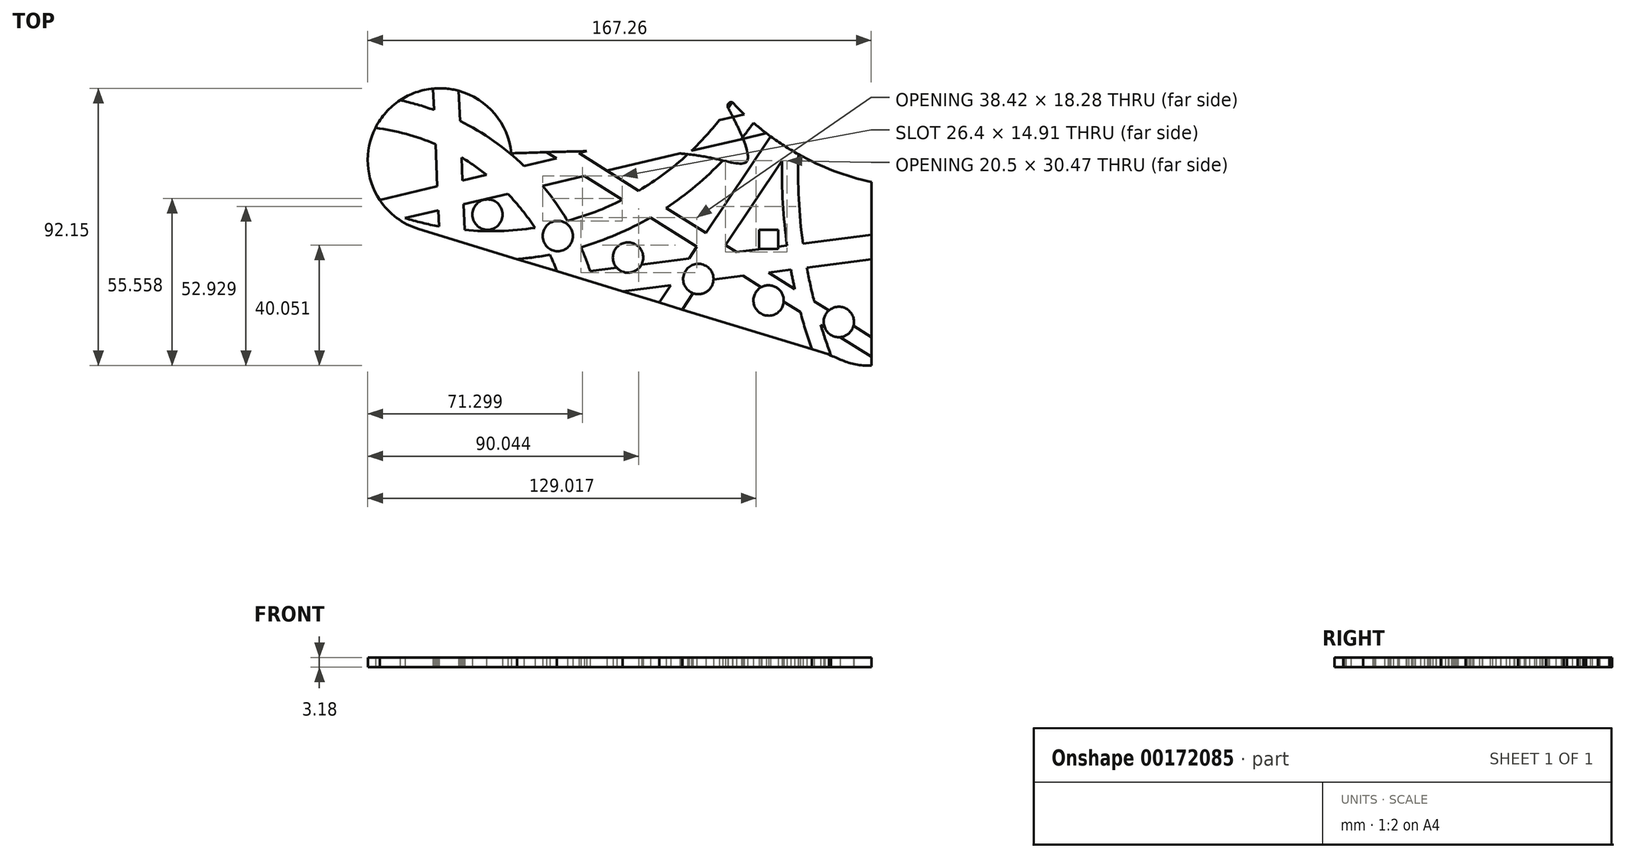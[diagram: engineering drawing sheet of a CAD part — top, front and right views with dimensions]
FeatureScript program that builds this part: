
annotation { "Feature Type Name" : "Feature", "Feature Type Description" : "" }
export const myFeature = defineFeature(function(context is Context, id is Id, definition is map)
    precondition{}
    {
        {
            var Q0;
            Q0=qCreatedBy(makeId("Top.planeOp"),FACE);
            var sketch = newSketch(context, id + "F0", { "sketchPlane" : qUnion([Q0])});
            skArc(sketch, "E0", {"start": v(-90.46, -15.28) * mm, "mid": v(-14.2, -9.68) * mm, "end": v(38.46, 45.77) * mm});
            skArc(sketch, "E1.0", {"start": v(-100.3, -1.2) * mm, "mid": v(-24.88, -3.77) * mm, "end": v(29.26, 48.8) * mm});
            skArc(sketch, "E2", {"start": v(51.31, 64.63) * mm, "mid": v(42.5, 3.49) * mm, "end": v(55.46, -56.9) * mm});
            skArc(sketch, "E3.0", {"start": v(46.25, 66.31) * mm, "mid": v(37.17, 3.3) * mm, "end": v(50.52, -58.93) * mm});
            skArc(sketch, "E4", {"start": v(-33.41, -40.98) * mm, "mid": v(-60.63, 8.15) * mm, "end": v(-114.4, 24.36) * mm});
            skArc(sketch, "E5.0", {"start": v(-23.07, -39.74) * mm, "mid": v(-54.1, 16.25) * mm, "end": v(-115.38, 34.73) * mm});
            skLineSegment(sketch, "E6.0", {"start": v(52.65, -51.2) * mm, "end": v(-83.61, -9.54) * mm});
            skArc(sketch, "E6.1", {"start": v(-52.83, 15.6) * mm, "mid": v(-91.75, 31.83) * mm, "end": v(-83.61, -9.54) * mm});
            skFitSpline(sketch, "E6.5", {"points": [v(52.65, -51.2) * mm, v(64.8, -54.91) * mm, v(80.38, -50.62) * mm, v(85.15, -44.27) * mm]});
            skLineSegment(sketch, "E6.6", {"start": v(66.1, 6.22) * mm, "end": v(66.1, -52.4) * mm});
            skPoint(sketch, "E7.visualSharp", {"position": v(13.9, 42.17) * mm});
            skArc(sketch, "E8", {"start": v(12.87, 42.18) * mm, "mid": v(44.36, 14.28) * mm, "end": v(85.15, 3.99) * mm});
            skFitSpline(sketch, "E9", {"points": [v(-52.83, 15.6) * mm, v(12.87, 42.18) * mm], "startDerivative": vector(194.61, -3.65) * mm, "endDerivative": vector(-37.72, 87.36) * mm});
            skLineSegment(sketch, "E10", {"start": v(66.73, 6.07) * mm, "end": v(66.73, -50.68) * mm});
            skLineSegment(sketch, "E11", {"start": v(66.73, -50.68) * mm, "end": v(66.73, -55.63) * mm});
            skArc(sketch, "E12", {"start": v(66.1, -52.4) * mm, "mid": v(66.43, -52.34) * mm, "end": v(66.73, -52.2) * mm});
            skSolve(sketch);
        }
        {
            var Q0;
            Q0=qCreatedBy(makeId("Top.planeOp"),FACE);
            var sketch = newSketch(context, id + "F1", { "sketchPlane" : qUnion([Q0])});
            skLineSegment(sketch, "E13", {"start": v(41.28, 19.45) * mm, "end": v(0, -42.12) * mm});
            skLineSegment(sketch, "E14", {"start": v(0, -42.12) * mm, "end": v(-6.32, -37.88) * mm});
            skLineSegment(sketch, "E15", {"start": v(-6.32, -37.88) * mm, "end": v(38.05, 28.32) * mm});
            skLineSegment(sketch, "E16", {"start": v(38.05, 28.32) * mm, "end": v(41.28, 19.45) * mm});
            skLineSegment(sketch, "E17", {"start": v(40.9, -75.03) * mm, "end": v(46.22, -72.68) * mm});
            skLineSegment(sketch, "E18", {"start": v(-56.42, -35.5) * mm, "end": v(132.52, -11.1) * mm});
            skLineSegment(sketch, "E19", {"start": v(132.52, -11.1) * mm, "end": v(131.24, -3.12) * mm});
            skLineSegment(sketch, "E20", {"start": v(131.24, -3.12) * mm, "end": v(-56.79, -27.4) * mm});
            skLineSegment(sketch, "E21", {"start": v(-56.79, -27.4) * mm, "end": v(-56.42, -35.5) * mm});
            skLineSegment(sketch, "E22", {"start": v(-71.95, 73.85) * mm, "end": v(-66.69, -48.5) * mm});
            skLineSegment(sketch, "E23", {"start": v(-66.69, -48.5) * mm, "end": v(-75.13, -48.86) * mm});
            skLineSegment(sketch, "E24", {"start": v(-75.13, -48.86) * mm, "end": v(-80.24, 69.83) * mm});
            skLineSegment(sketch, "E25", {"start": v(-80.24, 69.83) * mm, "end": v(-71.95, 73.85) * mm});
            skLineSegment(sketch, "E26", {"start": v(70.66, -54.45) * mm, "end": v(-45.44, 18.7) * mm});
            skLineSegment(sketch, "E27", {"start": v(-45.44, 18.7) * mm, "end": v(-42.5, 23.35) * mm});
            skLineSegment(sketch, "E28", {"start": v(-42.5, 23.35) * mm, "end": v(73.52, -49.75) * mm});
            skLineSegment(sketch, "E29", {"start": v(73.52, -49.75) * mm, "end": v(70.66, -54.45) * mm});
            skLineSegment(sketch, "E30", {"start": v(56.6, 28.12) * mm, "end": v(-113.4, -11.85) * mm});
            skLineSegment(sketch, "E31", {"start": v(-113.4, -11.85) * mm, "end": v(-115.19, -4.23) * mm});
            skLineSegment(sketch, "E32", {"start": v(-115.19, -4.23) * mm, "end": v(55.1, 35.8) * mm});
            skLineSegment(sketch, "E33", {"start": v(55.1, 35.8) * mm, "end": v(56.6, 28.12) * mm});
            skArc(sketch, "E34.0", {"start": v(-90.46, -15.28) * mm, "mid": v(-14.2, -9.68) * mm, "end": v(38.46, 45.77) * mm});
            skArc(sketch, "E34.1", {"start": v(-100.3, -1.2) * mm, "mid": v(-24.88, -3.77) * mm, "end": v(29.26, 48.8) * mm});
            skArc(sketch, "E34.2", {"start": v(51.31, 64.63) * mm, "mid": v(42.5, 3.49) * mm, "end": v(55.46, -56.9) * mm});
            skArc(sketch, "E34.3", {"start": v(46.25, 66.31) * mm, "mid": v(37.17, 3.3) * mm, "end": v(50.52, -58.93) * mm});
            skArc(sketch, "E34.4", {"start": v(-33.41, -40.98) * mm, "mid": v(-60.63, 8.15) * mm, "end": v(-114.4, 24.36) * mm});
            skArc(sketch, "E34.5", {"start": v(-23.07, -39.74) * mm, "mid": v(-54.1, 16.25) * mm, "end": v(-115.38, 34.73) * mm});
            skArc(sketch, "E35.0", {"start": v(-52.83, 15.6) * mm, "mid": v(-91.75, 31.83) * mm, "end": v(-83.61, -9.54) * mm});
            skFitSpline(sketch, "E35.1", {"points": [v(-52.83, 15.6) * mm, v(12.04, 14.39) * mm, v(25.44, 13.06) * mm, v(12.87, 42.18) * mm]});
            skArc(sketch, "E35.2", {"start": v(12.87, 42.18) * mm, "mid": v(44.36, 14.28) * mm, "end": v(85.15, 3.99) * mm});
            skLineSegment(sketch, "E35.3", {"start": v(66.1, 6.22) * mm, "end": v(66.1, -52.4) * mm});
            skFitSpline(sketch, "E35.4", {"points": [v(52.65, -51.2) * mm, v(64.8, -54.91) * mm, v(80.38, -50.62) * mm, v(85.15, -44.27) * mm]});
            skLineSegment(sketch, "E35.5", {"start": v(52.65, -51.2) * mm, "end": v(-83.61, -9.54) * mm});
            skLineSegment(sketch, "E36.0", {"start": v(66.73, 6.07) * mm, "end": v(66.73, -50.68) * mm});
            skLineSegment(sketch, "E37.0", {"start": v(66.73, -50.68) * mm, "end": v(66.73, -55.63) * mm});
            skArc(sketch, "E38.0", {"start": v(66.1, -52.4) * mm, "mid": v(66.43, -52.34) * mm, "end": v(66.73, -52.2) * mm});
            skSolve(sketch);
        }
        {
            var Q0;
            {var subQ0=sQuery(id+"F1.wireOp",EDGE,"E35.3");var subQ1=sQuery(id+"F1.wireOp",EDGE,"E26");var subQ2=makeQuery(id+"F1.imprint","INTERSECT",VERTEX,{"derivedFrom":[subQ1,subQ0]});Q0=makeQuery(id+"F1.imprint","IMPRINT",FACE,{"disambiguationData":[TD([[makeQuery(id+"F1.imprint","IMPRINT",EDGE,{"disambiguationData":[TD([[subQ2,-1.0]])],"derivedFrom":subQ1}),-1.0]])]});}
            var Q1;
            {var subQ0=sQuery(id+"F1.wireOp",EDGE,"E37.0");var subQ6=sQuery(id+"F1.wireOp",EDGE,"E26");var subQ9=makeQuery(id+"F1.imprint","INTERSECT",VERTEX,{"derivedFrom":[subQ6,subQ0]});Q1=makeQuery(id+"F1.imprint","IMPRINT",FACE,{"disambiguationData":[TD([[makeQuery(id+"F1.imprint","IMPRINT",EDGE,{"disambiguationData":[TD([[subQ9,-1.0]])],"derivedFrom":subQ6}),-1.0]])]});}
            var Q2;
            {var subQ0=sQuery(id+"F1.wireOp",EDGE,"E36.0");var subQ1=sQuery(id+"F1.wireOp",EDGE,"E18");var subQ2=makeQuery(id+"F1.imprint","INTERSECT",VERTEX,{"derivedFrom":[subQ1,subQ0]});Q2=makeQuery(id+"F1.imprint","IMPRINT",FACE,{"disambiguationData":[TD([[makeQuery(id+"F1.imprint","IMPRINT",EDGE,{"disambiguationData":[TD([[subQ2,1.0]])],"derivedFrom":subQ1}),1.0]])]});}
            var Q3;
            {var subQ0=sQuery(id+"F1.wireOp",EDGE,"E34.2");var subQ1=sQuery(id+"F1.wireOp",EDGE,"E18");var subQ2=makeQuery(id+"F1.imprint","INTERSECT",VERTEX,{"derivedFrom":[subQ1,subQ0]});Q3=makeQuery(id+"F1.imprint","IMPRINT",FACE,{"disambiguationData":[TD([[makeQuery(id+"F1.imprint","IMPRINT",EDGE,{"disambiguationData":[TD([[subQ2,-1.0]])],"derivedFrom":subQ1}),1.0]])]});}
            var Q4;
            {var subQ0=sQuery(id+"F1.wireOp",EDGE,"E34.2");var subQ1=sQuery(id+"F1.wireOp",EDGE,"E13");var subQ2=makeQuery(id+"F1.imprint","INTERSECT",VERTEX,{"derivedFrom":[subQ1,subQ0]});Q4=makeQuery(id+"F1.imprint","IMPRINT",FACE,{"disambiguationData":[TD([[makeQuery(id+"F1.imprint","IMPRINT",EDGE,{"disambiguationData":[TD([[subQ2,-1.0]])],"derivedFrom":subQ1}),-1.0]])]});}
            var Q5;
            {var subQ0=sQuery(id+"F1.wireOp",EDGE,"E34.3");var subQ1=sQuery(id+"F1.wireOp",EDGE,"E13");var subQ2=makeQuery(id+"F1.imprint","INTERSECT",VERTEX,{"derivedFrom":[subQ1,subQ0]});Q5=makeQuery(id+"F1.imprint","IMPRINT",FACE,{"disambiguationData":[TD([[makeQuery(id+"F1.imprint","IMPRINT",EDGE,{"disambiguationData":[TD([[subQ2,-1.0]])],"derivedFrom":subQ1}),-1.0]])]});}
            var Q6;
            {var subQ0=sQuery(id+"F1.wireOp",EDGE,"E34.2");var subQ1=sQuery(id+"F1.wireOp",EDGE,"E13");var subQ2=makeQuery(id+"F1.imprint","INTERSECT",VERTEX,{"derivedFrom":[subQ1,subQ0]});Q6=makeQuery(id+"F1.imprint","IMPRINT",FACE,{"disambiguationData":[TD([[makeQuery(id+"F1.imprint","IMPRINT",EDGE,{"disambiguationData":[TD([[subQ2,-1.0]])],"derivedFrom":subQ1}),1.0]])]});}
            var Q7;
            {var subQ0=sQuery(id+"F1.wireOp",EDGE,"E34.3");var subQ1=sQuery(id+"F1.wireOp",EDGE,"E18");var subQ2=makeQuery(id+"F1.imprint","INTERSECT",VERTEX,{"derivedFrom":[subQ1,subQ0]});Q7=makeQuery(id+"F1.imprint","IMPRINT",FACE,{"disambiguationData":[TD([[makeQuery(id+"F1.imprint","IMPRINT",EDGE,{"disambiguationData":[TD([[subQ2,-1.0]])],"derivedFrom":subQ1}),1.0]])]});}
            var Q8;
            {var subQ0=sQuery(id+"F1.wireOp",EDGE,"E34.3");var subQ1=sQuery(id+"F1.wireOp",EDGE,"E18");var subQ2=makeQuery(id+"F1.imprint","INTERSECT",VERTEX,{"derivedFrom":[subQ1,subQ0]});Q8=makeQuery(id+"F1.imprint","IMPRINT",FACE,{"disambiguationData":[TD([[makeQuery(id+"F1.imprint","IMPRINT",EDGE,{"disambiguationData":[TD([[subQ2,-1.0]])],"derivedFrom":subQ1}),-1.0]])]});}
            var Q9;
            {var subQ0=sQuery(id+"F1.wireOp",EDGE,"E34.2");var subQ1=sQuery(id+"F1.wireOp",EDGE,"E26");var subQ2=makeQuery(id+"F1.imprint","INTERSECT",VERTEX,{"derivedFrom":[subQ1,subQ0]});Q9=makeQuery(id+"F1.imprint","IMPRINT",FACE,{"disambiguationData":[TD([[makeQuery(id+"F1.imprint","IMPRINT",EDGE,{"disambiguationData":[TD([[subQ2,-1.0]])],"derivedFrom":subQ1}),-1.0]])]});}
            var Q10;
            {var subQ3=sQuery(id+"F1.wireOp",EDGE,"E34.2");var subQ7=sQuery(id+"F1.wireOp",EDGE,"E26");var subQ9=makeQuery(id+"F1.imprint","INTERSECT",VERTEX,{"derivedFrom":[subQ7,subQ3]});Q10=makeQuery(id+"F1.imprint","IMPRINT",FACE,{"disambiguationData":[TD([[makeQuery(id+"F1.imprint","IMPRINT",EDGE,{"disambiguationData":[TD([[subQ9,-1.0]])],"derivedFrom":subQ7}),1.0]])]});}
            var Q11;
            {var subQ0=sQuery(id+"F1.wireOp",EDGE,"E26");var subQ1=sQuery(id+"F1.wireOp",EDGE,"E18");var subQ2=makeQuery(id+"F1.imprint","INTERSECT",VERTEX,{"derivedFrom":[subQ1,subQ0]});Q11=makeQuery(id+"F1.imprint","IMPRINT",FACE,{"disambiguationData":[TD([[makeQuery(id+"F1.imprint","IMPRINT",EDGE,{"disambiguationData":[TD([[subQ2,-1.0]])],"derivedFrom":subQ1}),-1.0]])]});}
            var Q12;
            {var subQ0=sQuery(id+"F1.wireOp",EDGE,"E28");var subQ1=sQuery(id+"F1.wireOp",EDGE,"E18");var subQ2=makeQuery(id+"F1.imprint","INTERSECT",VERTEX,{"derivedFrom":[subQ1,subQ0]});Q12=makeQuery(id+"F1.imprint","IMPRINT",FACE,{"disambiguationData":[TD([[makeQuery(id+"F1.imprint","IMPRINT",EDGE,{"disambiguationData":[TD([[subQ2,-1.0]])],"derivedFrom":subQ1}),1.0]])]});}
            var Q13;
            {var subQ0=sQuery(id+"F1.wireOp",EDGE,"E20");var subQ1=sQuery(id+"F1.wireOp",EDGE,"E13");var subQ2=makeQuery(id+"F1.imprint","INTERSECT",VERTEX,{"derivedFrom":[subQ1,subQ0]});Q13=makeQuery(id+"F1.imprint","IMPRINT",FACE,{"disambiguationData":[TD([[makeQuery(id+"F1.imprint","IMPRINT",EDGE,{"disambiguationData":[TD([[subQ2,-1.0]])],"derivedFrom":subQ1}),1.0]])]});}
            var Q14;
            {var subQ0=sQuery(id+"F1.wireOp",EDGE,"E28");var subQ1=sQuery(id+"F1.wireOp",EDGE,"E13");var subQ2=makeQuery(id+"F1.imprint","INTERSECT",VERTEX,{"derivedFrom":[subQ1,subQ0]});Q14=makeQuery(id+"F1.imprint","IMPRINT",FACE,{"disambiguationData":[TD([[makeQuery(id+"F1.imprint","IMPRINT",EDGE,{"disambiguationData":[TD([[subQ2,-1.0]])],"derivedFrom":subQ1}),1.0]])]});}
            var Q15;
            {var subQ1=sQuery(id+"F1.wireOp",EDGE,"E13");var subQ7=sQuery(id+"F1.wireOp",EDGE,"E28");var subQ9=makeQuery(id+"F1.imprint","INTERSECT",VERTEX,{"derivedFrom":[subQ1,subQ7]});Q15=makeQuery(id+"F1.imprint","IMPRINT",FACE,{"disambiguationData":[TD([[makeQuery(id+"F1.imprint","IMPRINT",EDGE,{"disambiguationData":[TD([[subQ9,-1.0]])],"derivedFrom":subQ1}),-1.0]])]});}
            var Q16;
            {var subQ0=sQuery(id+"F1.wireOp",EDGE,"E26");var subQ1=sQuery(id+"F1.wireOp",EDGE,"E13");var subQ2=makeQuery(id+"F1.imprint","INTERSECT",VERTEX,{"derivedFrom":[subQ1,subQ0]});Q16=makeQuery(id+"F1.imprint","IMPRINT",FACE,{"disambiguationData":[TD([[makeQuery(id+"F1.imprint","IMPRINT",EDGE,{"disambiguationData":[TD([[subQ2,-1.0]])],"derivedFrom":subQ1}),1.0]])]});}
            var Q17;
            {var subQ0=sQuery(id+"F1.wireOp",EDGE,"E20");var subQ1=sQuery(id+"F1.wireOp",EDGE,"E13");var subQ2=makeQuery(id+"F1.imprint","INTERSECT",VERTEX,{"derivedFrom":[subQ1,subQ0]});Q17=makeQuery(id+"F1.imprint","IMPRINT",FACE,{"disambiguationData":[TD([[makeQuery(id+"F1.imprint","IMPRINT",EDGE,{"disambiguationData":[TD([[subQ2,-1.0]])],"derivedFrom":subQ1}),-1.0]])]});}
            var Q18;
            {var subQ1=sQuery(id+"F1.wireOp",EDGE,"E13");var subQ7=sQuery(id+"F1.wireOp",EDGE,"E26");var subQ9=makeQuery(id+"F1.imprint","INTERSECT",VERTEX,{"derivedFrom":[subQ1,subQ7]});Q18=makeQuery(id+"F1.imprint","IMPRINT",FACE,{"disambiguationData":[TD([[makeQuery(id+"F1.imprint","IMPRINT",EDGE,{"disambiguationData":[TD([[subQ9,-1.0]])],"derivedFrom":subQ1}),-1.0]])]});}
            var Q19;
            {var subQ0=sQuery(id+"F1.wireOp",EDGE,"E20");var subQ1=sQuery(id+"F1.wireOp",EDGE,"E15");var subQ2=makeQuery(id+"F1.imprint","INTERSECT",VERTEX,{"derivedFrom":[subQ1,subQ0]});Q19=makeQuery(id+"F1.imprint","IMPRINT",FACE,{"disambiguationData":[TD([[makeQuery(id+"F1.imprint","IMPRINT",EDGE,{"disambiguationData":[TD([[subQ2,-1.0]])],"derivedFrom":subQ1}),-1.0]])]});}
            var Q20;
            {var subQ0=sQuery(id+"F1.wireOp",EDGE,"E35.5");var subQ1=sQuery(id+"F1.wireOp",EDGE,"E13");var subQ2=makeQuery(id+"F1.imprint","INTERSECT",VERTEX,{"derivedFrom":[subQ1,subQ0]});Q20=makeQuery(id+"F1.imprint","IMPRINT",FACE,{"disambiguationData":[TD([[makeQuery(id+"F1.imprint","IMPRINT",EDGE,{"disambiguationData":[TD([[subQ2,1.0]])],"derivedFrom":subQ1}),-1.0]])]});}
            var Q21;
            {var subQ1=sQuery(id+"F1.wireOp",EDGE,"E18");var subQ3=sQuery(id+"F1.wireOp",EDGE,"E15");var subQ4=makeQuery(id+"F1.imprint","INTERSECT",VERTEX,{"derivedFrom":[subQ3,subQ1]});Q21=makeQuery(id+"F1.imprint","IMPRINT",FACE,{"disambiguationData":[TD([[makeQuery(id+"F1.imprint","IMPRINT",EDGE,{"disambiguationData":[TD([[subQ4,-1.0]])],"derivedFrom":subQ3}),1.0]])]});}
            var Q22;
            {var subQ0=sQuery(id+"F1.wireOp",EDGE,"E26");var subQ1=sQuery(id+"F1.wireOp",EDGE,"E15");var subQ2=makeQuery(id+"F1.imprint","INTERSECT",VERTEX,{"derivedFrom":[subQ1,subQ0]});Q22=makeQuery(id+"F1.imprint","IMPRINT",FACE,{"disambiguationData":[TD([[makeQuery(id+"F1.imprint","IMPRINT",EDGE,{"disambiguationData":[TD([[subQ2,-1.0]])],"derivedFrom":subQ1}),1.0]])]});}
            var Q23;
            {var subQ0=sQuery(id+"F1.wireOp",EDGE,"E34.1");var subQ1=sQuery(id+"F1.wireOp",EDGE,"E28");var subQ2=makeQuery(id+"F1.imprint","INTERSECT",VERTEX,{"derivedFrom":[subQ1,subQ0]});Q23=makeQuery(id+"F1.imprint","IMPRINT",FACE,{"disambiguationData":[TD([[makeQuery(id+"F1.imprint","IMPRINT",EDGE,{"disambiguationData":[TD([[subQ2,-1.0]])],"derivedFrom":subQ1}),1.0]])]});}
            var Q24;
            {var subQ1=sQuery(id+"F1.wireOp",EDGE,"E30");var subQ9=sQuery(id+"F1.wireOp",EDGE,"E34.0");var subQ10=makeQuery(id+"F1.imprint","INTERSECT",VERTEX,{"derivedFrom":[subQ1,subQ9]});Q24=makeQuery(id+"F1.imprint","IMPRINT",FACE,{"disambiguationData":[TD([[makeQuery(id+"F1.imprint","IMPRINT",EDGE,{"disambiguationData":[TD([[subQ10,-1.0]])],"derivedFrom":subQ1}),-1.0]])]});}
            var Q25;
            {var subQ0=sQuery(id+"F1.wireOp",EDGE,"E35.2");var subQ1=sQuery(id+"F1.wireOp",EDGE,"E32");var subQ2=makeQuery(id+"F1.imprint","INTERSECT",VERTEX,{"derivedFrom":[subQ1,subQ0]});Q25=makeQuery(id+"F1.imprint","IMPRINT",FACE,{"disambiguationData":[TD([[makeQuery(id+"F1.imprint","IMPRINT",EDGE,{"disambiguationData":[TD([[subQ2,1.0]])],"derivedFrom":subQ1}),1.0]])]});}
            var Q26;
            {var subQ0=sQuery(id+"F1.wireOp",EDGE,"E35.1");var subQ1=sQuery(id+"F1.wireOp",EDGE,"E28");var subQ2=makeQuery(id+"F1.imprint","INTERSECT",VERTEX,{"derivedFrom":[subQ1,subQ0]});Q26=makeQuery(id+"F1.imprint","IMPRINT",FACE,{"disambiguationData":[TD([[makeQuery(id+"F1.imprint","IMPRINT",EDGE,{"disambiguationData":[TD([[subQ2,-1.0]])],"derivedFrom":subQ1}),1.0]])]});}
            var Q27;
            {var subQ0=sQuery(id+"F1.wireOp",EDGE,"E34.0");var subQ1=sQuery(id+"F1.wireOp",EDGE,"E26");var subQ2=makeQuery(id+"F1.imprint","INTERSECT",VERTEX,{"derivedFrom":[subQ1,subQ0]});Q27=makeQuery(id+"F1.imprint","IMPRINT",FACE,{"disambiguationData":[TD([[makeQuery(id+"F1.imprint","IMPRINT",EDGE,{"disambiguationData":[TD([[subQ2,-1.0]])],"derivedFrom":subQ1}),-1.0]])]});}
            var Q28;
            {var subQ0=sQuery(id+"F1.wireOp",EDGE,"E34.1");var subQ1=sQuery(id+"F1.wireOp",EDGE,"E26");var subQ2=makeQuery(id+"F1.imprint","INTERSECT",VERTEX,{"derivedFrom":[subQ1,subQ0]});Q28=makeQuery(id+"F1.imprint","IMPRINT",FACE,{"disambiguationData":[TD([[makeQuery(id+"F1.imprint","IMPRINT",EDGE,{"disambiguationData":[TD([[subQ2,-1.0]])],"derivedFrom":subQ1}),-1.0]])]});}
            var Q29;
            {var subQ0=sQuery(id+"F1.wireOp",EDGE,"E30");var subQ1=sQuery(id+"F1.wireOp",EDGE,"E26");var subQ2=makeQuery(id+"F1.imprint","INTERSECT",VERTEX,{"derivedFrom":[subQ1,subQ0]});Q29=makeQuery(id+"F1.imprint","IMPRINT",FACE,{"disambiguationData":[TD([[makeQuery(id+"F1.imprint","IMPRINT",EDGE,{"disambiguationData":[TD([[subQ2,-1.0]])],"derivedFrom":subQ1}),-1.0]])]});}
            var Q30;
            {var subQ0=sQuery(id+"F1.wireOp",EDGE,"E35.1");var subQ1=sQuery(id+"F1.wireOp",EDGE,"E26");var subQ2=makeQuery(id+"F1.imprint","INTERSECT",VERTEX,{"derivedFrom":[subQ1,subQ0]});Q30=makeQuery(id+"F1.imprint","IMPRINT",FACE,{"disambiguationData":[TD([[makeQuery(id+"F1.imprint","IMPRINT",EDGE,{"disambiguationData":[TD([[subQ2,1.0]])],"derivedFrom":subQ1}),-1.0]])]});}
            var Q31;
            {var subQ0=sQuery(id+"F1.wireOp",EDGE,"E30");var subQ1=sQuery(id+"F1.wireOp",EDGE,"E26");var subQ2=makeQuery(id+"F1.imprint","INTERSECT",VERTEX,{"derivedFrom":[subQ1,subQ0]});Q31=makeQuery(id+"F1.imprint","IMPRINT",FACE,{"disambiguationData":[TD([[makeQuery(id+"F1.imprint","IMPRINT",EDGE,{"disambiguationData":[TD([[subQ2,-1.0]])],"derivedFrom":subQ1}),1.0]])]});}
            var Q32;
            {var subQ0=sQuery(id+"F1.wireOp",EDGE,"E34.0");var subQ1=sQuery(id+"F1.wireOp",EDGE,"E26");var subQ2=makeQuery(id+"F1.imprint","INTERSECT",VERTEX,{"derivedFrom":[subQ1,subQ0]});Q32=makeQuery(id+"F1.imprint","IMPRINT",FACE,{"disambiguationData":[TD([[makeQuery(id+"F1.imprint","IMPRINT",EDGE,{"disambiguationData":[TD([[subQ2,-1.0]])],"derivedFrom":subQ1}),1.0]])]});}
            var Q33;
            {var subQ0=sQuery(id+"F1.wireOp",EDGE,"E34.5");var subQ1=sQuery(id+"F1.wireOp",EDGE,"E20");var subQ2=makeQuery(id+"F1.imprint","INTERSECT",VERTEX,{"derivedFrom":[subQ1,subQ0]});Q33=makeQuery(id+"F1.imprint","IMPRINT",FACE,{"disambiguationData":[TD([[makeQuery(id+"F1.imprint","IMPRINT",EDGE,{"disambiguationData":[TD([[subQ2,-1.0]])],"derivedFrom":subQ1}),1.0]])]});}
            var Q34;
            {var subQ5=sQuery(id+"F1.wireOp",EDGE,"E34.5");var subQ7=sQuery(id+"F1.wireOp",EDGE,"E20");var subQ8=makeQuery(id+"F1.imprint","INTERSECT",VERTEX,{"derivedFrom":[subQ7,subQ5]});Q34=makeQuery(id+"F1.imprint","IMPRINT",FACE,{"disambiguationData":[TD([[makeQuery(id+"F1.imprint","IMPRINT",EDGE,{"disambiguationData":[TD([[subQ8,-1.0]])],"derivedFrom":subQ7}),-1.0]])]});}
            var Q35;
            {var subQ0=sQuery(id+"F1.wireOp",EDGE,"E34.4");var subQ1=sQuery(id+"F1.wireOp",EDGE,"E34.0");var subQ2=makeQuery(id+"F1.imprint","INTERSECT",VERTEX,{"derivedFrom":[subQ1,subQ0]});Q35=makeQuery(id+"F1.imprint","IMPRINT",FACE,{"disambiguationData":[TD([[makeQuery(id+"F1.imprint","IMPRINT",EDGE,{"disambiguationData":[TD([[subQ2,-1.0]])],"derivedFrom":subQ1}),1.0]])]});}
            var Q36;
            {var subQ0=sQuery(id+"F1.wireOp",EDGE,"E34.5");var subQ1=sQuery(id+"F1.wireOp",EDGE,"E30");var subQ2=makeQuery(id+"F1.imprint","INTERSECT",VERTEX,{"derivedFrom":[subQ1,subQ0]});Q36=makeQuery(id+"F1.imprint","IMPRINT",FACE,{"disambiguationData":[TD([[makeQuery(id+"F1.imprint","IMPRINT",EDGE,{"disambiguationData":[TD([[subQ2,-1.0]])],"derivedFrom":subQ1}),1.0]])]});}
            var Q37;
            {var subQ0=sQuery(id+"F1.wireOp",EDGE,"E34.5");var subQ1=sQuery(id+"F1.wireOp",EDGE,"E30");var subQ2=makeQuery(id+"F1.imprint","INTERSECT",VERTEX,{"derivedFrom":[subQ1,subQ0]});Q37=makeQuery(id+"F1.imprint","IMPRINT",FACE,{"disambiguationData":[TD([[makeQuery(id+"F1.imprint","IMPRINT",EDGE,{"disambiguationData":[TD([[subQ2,-1.0]])],"derivedFrom":subQ1}),-1.0]])]});}
            var Q38;
            {var subQ0=sQuery(id+"F1.wireOp",EDGE,"E34.5");var subQ1=sQuery(id+"F1.wireOp",EDGE,"E22");var subQ2=makeQuery(id+"F1.imprint","INTERSECT",VERTEX,{"derivedFrom":[subQ1,subQ0]});Q38=makeQuery(id+"F1.imprint","IMPRINT",FACE,{"disambiguationData":[TD([[makeQuery(id+"F1.imprint","IMPRINT",EDGE,{"disambiguationData":[TD([[subQ2,-1.0]])],"derivedFrom":subQ1}),1.0]])]});}
            var Q39;
            {var subQ0=sQuery(id+"F1.wireOp",EDGE,"E34.5");var subQ1=sQuery(id+"F1.wireOp",EDGE,"E22");var subQ2=makeQuery(id+"F1.imprint","INTERSECT",VERTEX,{"derivedFrom":[subQ1,subQ0]});Q39=makeQuery(id+"F1.imprint","IMPRINT",FACE,{"disambiguationData":[TD([[makeQuery(id+"F1.imprint","IMPRINT",EDGE,{"disambiguationData":[TD([[subQ2,-1.0]])],"derivedFrom":subQ1}),-1.0]])]});}
            var Q40;
            {var subQ0=sQuery(id+"F1.wireOp",EDGE,"E35.0");var subQ1=sQuery(id+"F1.wireOp",EDGE,"E22");var subQ2=makeQuery(id+"F1.imprint","INTERSECT",VERTEX,{"derivedFrom":[subQ1,subQ0]});Q40=makeQuery(id+"F1.imprint","IMPRINT",FACE,{"disambiguationData":[TD([[makeQuery(id+"F1.imprint","IMPRINT",EDGE,{"disambiguationData":[TD([[subQ2,-1.0]])],"derivedFrom":subQ1}),-1.0]])]});}
            var Q41;
            {var subQ0=sQuery(id+"F1.wireOp",EDGE,"E34.4");var subQ1=sQuery(id+"F1.wireOp",EDGE,"E24");var subQ2=makeQuery(id+"F1.imprint","INTERSECT",VERTEX,{"derivedFrom":[subQ1,subQ0]});Q41=makeQuery(id+"F1.imprint","IMPRINT",FACE,{"disambiguationData":[TD([[makeQuery(id+"F1.imprint","IMPRINT",EDGE,{"disambiguationData":[TD([[subQ2,-1.0]])],"derivedFrom":subQ1}),1.0]])]});}
            var Q42;
            {var subQ0=sQuery(id+"F1.wireOp",EDGE,"E34.4");var subQ1=sQuery(id+"F1.wireOp",EDGE,"E22");var subQ2=makeQuery(id+"F1.imprint","INTERSECT",VERTEX,{"derivedFrom":[subQ1,subQ0]});Q42=makeQuery(id+"F1.imprint","IMPRINT",FACE,{"disambiguationData":[TD([[makeQuery(id+"F1.imprint","IMPRINT",EDGE,{"disambiguationData":[TD([[subQ2,-1.0]])],"derivedFrom":subQ1}),-1.0]])]});}
            var Q43;
            {var subQ0=sQuery(id+"F1.wireOp",EDGE,"E30");var subQ1=sQuery(id+"F1.wireOp",EDGE,"E24");var subQ2=makeQuery(id+"F1.imprint","INTERSECT",VERTEX,{"derivedFrom":[subQ1,subQ0]});Q43=makeQuery(id+"F1.imprint","IMPRINT",FACE,{"disambiguationData":[TD([[makeQuery(id+"F1.imprint","IMPRINT",EDGE,{"disambiguationData":[TD([[subQ2,-1.0]])],"derivedFrom":subQ1}),1.0]])]});}
            var Q44;
            {var subQ0=sQuery(id+"F1.wireOp",EDGE,"E32");var subQ1=sQuery(id+"F1.wireOp",EDGE,"E22");var subQ2=makeQuery(id+"F1.imprint","INTERSECT",VERTEX,{"derivedFrom":[subQ1,subQ0]});Q44=makeQuery(id+"F1.imprint","IMPRINT",FACE,{"disambiguationData":[TD([[makeQuery(id+"F1.imprint","IMPRINT",EDGE,{"disambiguationData":[TD([[subQ2,-1.0]])],"derivedFrom":subQ1}),-1.0]])]});}
            var Q45;
            {var subQ0=sQuery(id+"F1.wireOp",EDGE,"E32");var subQ1=sQuery(id+"F1.wireOp",EDGE,"E22");var subQ2=makeQuery(id+"F1.imprint","INTERSECT",VERTEX,{"derivedFrom":[subQ1,subQ0]});Q45=makeQuery(id+"F1.imprint","IMPRINT",FACE,{"disambiguationData":[TD([[makeQuery(id+"F1.imprint","IMPRINT",EDGE,{"disambiguationData":[TD([[subQ2,-1.0]])],"derivedFrom":subQ1}),1.0]])]});}
            var Q46;
            {var subQ0=sQuery(id+"F1.wireOp",EDGE,"E30");var subQ1=sQuery(id+"F1.wireOp",EDGE,"E22");var subQ2=makeQuery(id+"F1.imprint","INTERSECT",VERTEX,{"derivedFrom":[subQ1,subQ0]});Q46=makeQuery(id+"F1.imprint","IMPRINT",FACE,{"disambiguationData":[TD([[makeQuery(id+"F1.imprint","IMPRINT",EDGE,{"disambiguationData":[TD([[subQ2,-1.0]])],"derivedFrom":subQ1}),-1.0]])]});}
            var Q47;
            {var subQ0=sQuery(id+"F1.wireOp",EDGE,"E35.5");var subQ1=sQuery(id+"F1.wireOp",EDGE,"E34.0");var subQ2=makeQuery(id+"F1.imprint","INTERSECT",VERTEX,{"derivedFrom":[subQ1,subQ0]});Q47=makeQuery(id+"F1.imprint","IMPRINT",FACE,{"disambiguationData":[TD([[makeQuery(id+"F1.imprint","IMPRINT",EDGE,{"disambiguationData":[TD([[subQ2,-1.0]])],"derivedFrom":subQ1}),1.0]])]});}
            var Q48;
            {var subQ1=sQuery(id+"F1.wireOp",EDGE,"E13");var subQ5=sQuery(id+"F1.wireOp",EDGE,"E35.2");var subQ8=makeQuery(id+"F1.imprint","INTERSECT",VERTEX,{"derivedFrom":[subQ1,subQ5]});Q48=makeQuery(id+"F1.imprint","IMPRINT",FACE,{"disambiguationData":[TD([[makeQuery(id+"F1.imprint","IMPRINT",EDGE,{"disambiguationData":[TD([[subQ8,-1.0]])],"derivedFrom":subQ1}),1.0]])]});}
            var Q49;
            {var subQ0=sQuery(id+"F1.wireOp",EDGE,"E35.2");var subQ1=sQuery(id+"F1.wireOp",EDGE,"E30");var subQ2=makeQuery(id+"F1.imprint","INTERSECT",VERTEX,{"derivedFrom":[subQ1,subQ0]});Q49=makeQuery(id+"F1.imprint","IMPRINT",FACE,{"disambiguationData":[TD([[makeQuery(id+"F1.imprint","IMPRINT",EDGE,{"disambiguationData":[TD([[subQ2,-1.0]])],"derivedFrom":subQ1}),-1.0]])]});}
            var Q50;
            {var subQ0=sQuery(id+"F1.wireOp",EDGE,"E34.1");var subQ1=sQuery(id+"F1.wireOp",EDGE,"E22");var subQ2=makeQuery(id+"F1.imprint","INTERSECT",VERTEX,{"derivedFrom":[subQ1,subQ0]});Q50=makeQuery(id+"F1.imprint","IMPRINT",FACE,{"disambiguationData":[TD([[makeQuery(id+"F1.imprint","IMPRINT",EDGE,{"disambiguationData":[TD([[subQ2,-1.0]])],"derivedFrom":subQ1}),-1.0]])]});}
            var Q51;
            {var subQ0=sQuery(id+"F1.wireOp",EDGE,"E35.5");var subQ6=sQuery(id+"F1.wireOp",EDGE,"E24");var subQ9=makeQuery(id+"F1.imprint","INTERSECT",VERTEX,{"derivedFrom":[subQ6,subQ0]});Q51=makeQuery(id+"F1.imprint","IMPRINT",FACE,{"disambiguationData":[TD([[makeQuery(id+"F1.imprint","IMPRINT",EDGE,{"disambiguationData":[TD([[subQ9,-1.0]])],"derivedFrom":subQ6}),1.0]])]});}
            var Q52;
            {var subQ0=sQuery(id+"F1.wireOp",EDGE,"E35.0");var subQ1=sQuery(id+"F1.wireOp",EDGE,"E30");var subQ2=makeQuery(id+"F1.imprint","INTERSECT",VERTEX,{"derivedFrom":[subQ1,subQ0]});Q52=makeQuery(id+"F1.imprint","IMPRINT",FACE,{"disambiguationData":[TD([[makeQuery(id+"F1.imprint","IMPRINT",EDGE,{"disambiguationData":[TD([[subQ2,1.0]])],"derivedFrom":subQ1}),-1.0]])]});}
            extrude(context, id + "F2", {"entities" : qUnion([Q0, Q1, Q2, Q3, Q4, Q5, Q6, Q7, Q8, Q9, Q10, Q11, Q12, Q13, Q14, Q15, Q16, Q17, Q18, Q19, Q20, Q21, Q22, Q23, Q24, Q25, Q26, Q27, Q28, Q29, Q30, Q31, Q32, Q33, Q34, Q35, Q36, Q37, Q38, Q39, Q40, Q41, Q42, Q43, Q44, Q45, Q46, Q47, Q48, Q49, Q50, Q51, Q52]), "depth" : 3.17 * mm});
        }
        {
            var Q0;
            {var subQ0=sQuery(id+"F1.wireOp",EDGE,"E34.2");var subQ1=sQuery(id+"F1.wireOp",EDGE,"E18");var subQ2=makeQuery(id+"F1.imprint","INTERSECT",VERTEX,{"derivedFrom":[subQ1,subQ0]});Q0=makeQuery(id+"F1.imprint","IMPRINT",FACE,{"disambiguationData":[TD([[makeQuery(id+"F1.imprint","IMPRINT",EDGE,{"disambiguationData":[TD([[subQ2,-1.0]])],"derivedFrom":subQ1}),-1.0]])]});}
            var Q1;
            {var subQ0=sQuery(id+"F1.wireOp",EDGE,"E34.3");var subQ1=sQuery(id+"F1.wireOp",EDGE,"E13");var subQ2=makeQuery(id+"F1.imprint","INTERSECT",VERTEX,{"derivedFrom":[subQ1,subQ0]});Q1=makeQuery(id+"F1.imprint","IMPRINT",FACE,{"disambiguationData":[TD([[makeQuery(id+"F1.imprint","IMPRINT",EDGE,{"disambiguationData":[TD([[subQ2,-1.0]])],"derivedFrom":subQ1}),1.0]])]});}
            var Q2;
            {var subQ0=sQuery(id+"F1.wireOp",EDGE,"E28");var subQ1=sQuery(id+"F1.wireOp",EDGE,"E18");var subQ2=makeQuery(id+"F1.imprint","INTERSECT",VERTEX,{"derivedFrom":[subQ1,subQ0]});Q2=makeQuery(id+"F1.imprint","IMPRINT",FACE,{"disambiguationData":[TD([[makeQuery(id+"F1.imprint","IMPRINT",EDGE,{"disambiguationData":[TD([[subQ2,-1.0]])],"derivedFrom":subQ1}),-1.0]])]});}
            var Q3;
            {var subQ5=sQuery(id+"F1.wireOp",EDGE,"E13");var subQ7=sQuery(id+"F1.wireOp",EDGE,"E35.5");var subQ9=makeQuery(id+"F1.imprint","INTERSECT",VERTEX,{"derivedFrom":[subQ5,subQ7]});Q3=makeQuery(id+"F1.imprint","IMPRINT",FACE,{"disambiguationData":[TD([[makeQuery(id+"F1.imprint","IMPRINT",EDGE,{"disambiguationData":[TD([[subQ9,1.0]])],"derivedFrom":subQ5}),1.0]])]});}
            var Q4;
            {var subQ0=sQuery(id+"F1.wireOp",EDGE,"E35.3");var subQ1=sQuery(id+"F1.wireOp",EDGE,"E26");var subQ2=makeQuery(id+"F1.imprint","INTERSECT",VERTEX,{"derivedFrom":[subQ1,subQ0]});Q4=makeQuery(id+"F1.imprint","IMPRINT",FACE,{"disambiguationData":[TD([[makeQuery(id+"F1.imprint","IMPRINT",EDGE,{"disambiguationData":[TD([[subQ2,-1.0]])],"derivedFrom":subQ1}),1.0]])]});}
            var Q5;
            {var subQ0=sQuery(id+"F1.wireOp",EDGE,"E35.3");var subQ1=sQuery(id+"F1.wireOp",EDGE,"E20");var subQ2=makeQuery(id+"F1.imprint","INTERSECT",VERTEX,{"derivedFrom":[subQ1,subQ0]});Q5=makeQuery(id+"F1.imprint","IMPRINT",FACE,{"disambiguationData":[TD([[makeQuery(id+"F1.imprint","IMPRINT",EDGE,{"disambiguationData":[TD([[subQ2,-1.0]])],"derivedFrom":subQ1}),-1.0]])]});}
            var Q6;
            {var subQ0=sQuery(id+"F1.wireOp",EDGE,"E36.0");var subQ1=sQuery(id+"F1.wireOp",EDGE,"E20");var subQ2=makeQuery(id+"F1.imprint","INTERSECT",VERTEX,{"derivedFrom":[subQ1,subQ0]});Q6=makeQuery(id+"F1.imprint","IMPRINT",FACE,{"disambiguationData":[TD([[makeQuery(id+"F1.imprint","IMPRINT",EDGE,{"disambiguationData":[TD([[subQ2,-1.0]])],"derivedFrom":subQ1}),-1.0]])]});}
            var Q7;
            {var subQ0=sQuery(id+"F1.wireOp",EDGE,"E36.0");var subQ1=sQuery(id+"F1.wireOp",EDGE,"E18");var subQ2=makeQuery(id+"F1.imprint","INTERSECT",VERTEX,{"derivedFrom":[subQ1,subQ0]});Q7=makeQuery(id+"F1.imprint","IMPRINT",FACE,{"disambiguationData":[TD([[makeQuery(id+"F1.imprint","IMPRINT",EDGE,{"disambiguationData":[TD([[subQ2,1.0]])],"derivedFrom":subQ1}),-1.0]])]});}
            var Q8;
            {var subQ5=sQuery(id+"F1.wireOp",EDGE,"E38.0");Q8=makeQuery(id+"F1.imprint","IMPRINT",FACE,{"disambiguationData":[TD([[makeQuery(id+"F1.imprint","IMPRINT",EDGE,{"derivedFrom":subQ5}),1.0]])]});}
            extrude(context, id + "F3", {"entities" : qUnion([Q0, Q1, Q2, Q3, Q4, Q5, Q6, Q7, Q8]), "depth" : 3.17 * mm});
        }
        {
            var Q0;
            {var subQ0=sQuery(id+"F1.wireOp",EDGE,"E34.4");var subQ1=sQuery(id+"F1.wireOp",EDGE,"E22");var subQ2=makeQuery(id+"F1.imprint","INTERSECT",VERTEX,{"derivedFrom":[subQ1,subQ0]});Q0=makeQuery(id+"F1.imprint","IMPRINT",FACE,{"disambiguationData":[TD([[makeQuery(id+"F1.imprint","IMPRINT",EDGE,{"disambiguationData":[TD([[subQ2,-1.0]])],"derivedFrom":subQ1}),1.0]])]});}
            var Q1;
            {var subQ0=sQuery(id+"F1.wireOp",EDGE,"E32");var subQ1=sQuery(id+"F1.wireOp",EDGE,"E24");var subQ2=makeQuery(id+"F1.imprint","INTERSECT",VERTEX,{"derivedFrom":[subQ1,subQ0]});Q1=makeQuery(id+"F1.imprint","IMPRINT",FACE,{"disambiguationData":[TD([[makeQuery(id+"F1.imprint","IMPRINT",EDGE,{"disambiguationData":[TD([[subQ2,-1.0]])],"derivedFrom":subQ1}),1.0]])]});}
            var Q2;
            {var subQ0=sQuery(id+"F1.wireOp",EDGE,"E35.0");var subQ1=sQuery(id+"F1.wireOp",EDGE,"E24");var subQ2=makeQuery(id+"F1.imprint","INTERSECT",VERTEX,{"derivedFrom":[subQ1,subQ0]});Q2=makeQuery(id+"F1.imprint","IMPRINT",FACE,{"disambiguationData":[TD([[makeQuery(id+"F1.imprint","IMPRINT",EDGE,{"disambiguationData":[TD([[subQ2,1.0]])],"derivedFrom":subQ1}),1.0]])]});}
            var Q3;
            {var subQ0=sQuery(id+"F1.wireOp",EDGE,"E35.0");var subQ1=sQuery(id+"F1.wireOp",EDGE,"E24");var subQ2=makeQuery(id+"F1.imprint","INTERSECT",VERTEX,{"derivedFrom":[subQ1,subQ0]});Q3=makeQuery(id+"F1.imprint","IMPRINT",FACE,{"disambiguationData":[TD([[makeQuery(id+"F1.imprint","IMPRINT",EDGE,{"disambiguationData":[TD([[subQ2,1.0]])],"derivedFrom":subQ1}),1.0]])]});}
            var Q4;
            {var subQ0=sQuery(id+"F1.wireOp",EDGE,"E34.4");var subQ1=sQuery(id+"F1.wireOp",EDGE,"E22");var subQ2=makeQuery(id+"F1.imprint","INTERSECT",VERTEX,{"derivedFrom":[subQ1,subQ0]});Q4=makeQuery(id+"F1.imprint","IMPRINT",FACE,{"disambiguationData":[TD([[makeQuery(id+"F1.imprint","IMPRINT",EDGE,{"disambiguationData":[TD([[subQ2,-1.0]])],"derivedFrom":subQ1}),1.0]])]});}
            var Q5;
            {var subQ0=sQuery(id+"F1.wireOp",EDGE,"E30");var subQ1=sQuery(id+"F1.wireOp",EDGE,"E22");var subQ2=makeQuery(id+"F1.imprint","INTERSECT",VERTEX,{"derivedFrom":[subQ1,subQ0]});Q5=makeQuery(id+"F1.imprint","IMPRINT",FACE,{"disambiguationData":[TD([[makeQuery(id+"F1.imprint","IMPRINT",EDGE,{"disambiguationData":[TD([[subQ2,-1.0]])],"derivedFrom":subQ1}),1.0]])]});}
            var Q6;
            {var subQ0=sQuery(id+"F1.wireOp",EDGE,"E34.1");var subQ1=sQuery(id+"F1.wireOp",EDGE,"E26");var subQ2=makeQuery(id+"F1.imprint","INTERSECT",VERTEX,{"derivedFrom":[subQ1,subQ0]});Q6=makeQuery(id+"F1.imprint","IMPRINT",FACE,{"disambiguationData":[TD([[makeQuery(id+"F1.imprint","IMPRINT",EDGE,{"disambiguationData":[TD([[subQ2,-1.0]])],"derivedFrom":subQ1}),1.0]])]});}
            var Q7;
            {var subQ5=sQuery(id+"F1.wireOp",EDGE,"E20");var subQ6=sQuery(id+"F1.wireOp",EDGE,"E15");var subQ7=makeQuery(id+"F1.imprint","INTERSECT",VERTEX,{"derivedFrom":[subQ6,subQ5]});Q7=makeQuery(id+"F1.imprint","IMPRINT",FACE,{"disambiguationData":[TD([[makeQuery(id+"F1.imprint","IMPRINT",EDGE,{"disambiguationData":[TD([[subQ7,-1.0]])],"derivedFrom":subQ6}),1.0]])]});}
            var Q8;
            {var subQ0=sQuery(id+"F1.wireOp",EDGE,"E35.5");var subQ1=sQuery(id+"F1.wireOp",EDGE,"E15");var subQ2=makeQuery(id+"F1.imprint","INTERSECT",VERTEX,{"derivedFrom":[subQ1,subQ0]});Q8=makeQuery(id+"F1.imprint","IMPRINT",FACE,{"disambiguationData":[TD([[makeQuery(id+"F1.imprint","IMPRINT",EDGE,{"disambiguationData":[TD([[subQ2,-1.0]])],"derivedFrom":subQ1}),1.0]])]});}
            var Q9;
            {var subQ0=sQuery(id+"F1.wireOp",EDGE,"E28");var subQ1=sQuery(id+"F1.wireOp",EDGE,"E15");var subQ2=makeQuery(id+"F1.imprint","INTERSECT",VERTEX,{"derivedFrom":[subQ1,subQ0]});Q9=makeQuery(id+"F1.imprint","IMPRINT",FACE,{"disambiguationData":[TD([[makeQuery(id+"F1.imprint","IMPRINT",EDGE,{"disambiguationData":[TD([[subQ2,-1.0]])],"derivedFrom":subQ1}),1.0]])]});}
            var Q10;
            {var subQ0=sQuery(id+"F1.wireOp",EDGE,"E28");var subQ1=sQuery(id+"F1.wireOp",EDGE,"E15");var subQ2=makeQuery(id+"F1.imprint","INTERSECT",VERTEX,{"derivedFrom":[subQ1,subQ0]});Q10=makeQuery(id+"F1.imprint","IMPRINT",FACE,{"disambiguationData":[TD([[makeQuery(id+"F1.imprint","IMPRINT",EDGE,{"disambiguationData":[TD([[subQ2,-1.0]])],"derivedFrom":subQ1}),1.0]])]});}
            var Q11;
            {var subQ1=sQuery(id+"F1.wireOp",EDGE,"E22");var subQ6=sQuery(id+"F1.wireOp",EDGE,"E35.0");var subQ11=makeQuery(id+"F1.imprint","INTERSECT",VERTEX,{"derivedFrom":[subQ1,subQ6]});Q11=makeQuery(id+"F1.imprint","IMPRINT",FACE,{"disambiguationData":[TD([[makeQuery(id+"F1.imprint","IMPRINT",EDGE,{"disambiguationData":[TD([[subQ11,-1.0]])],"derivedFrom":subQ1}),1.0]])]});}
            var Q12;
            {var subQ0=sQuery(id+"F1.wireOp",EDGE,"E30");var subQ1=sQuery(id+"F1.wireOp",EDGE,"E28");var subQ2=makeQuery(id+"F1.imprint","INTERSECT",VERTEX,{"derivedFrom":[subQ1,subQ0]});Q12=makeQuery(id+"F1.imprint","IMPRINT",FACE,{"disambiguationData":[TD([[makeQuery(id+"F1.imprint","IMPRINT",EDGE,{"disambiguationData":[TD([[subQ2,-1.0]])],"derivedFrom":subQ1}),1.0]])]});}
            var Q13;
            {var subQ0=sQuery(id+"F1.wireOp",EDGE,"E35.2");var subQ1=sQuery(id+"F1.wireOp",EDGE,"E34.1");var subQ2=makeQuery(id+"F1.imprint","INTERSECT",VERTEX,{"derivedFrom":[subQ1,subQ0]});Q13=makeQuery(id+"F1.imprint","IMPRINT",FACE,{"disambiguationData":[TD([[makeQuery(id+"F1.imprint","IMPRINT",EDGE,{"disambiguationData":[TD([[subQ2,1.0]])],"derivedFrom":subQ1}),1.0]])]});}
            var Q14;
            {var subQ0=sQuery(id+"F1.wireOp",EDGE,"E35.5");var subQ1=sQuery(id+"F1.wireOp",EDGE,"E34.0");var subQ2=makeQuery(id+"F1.imprint","INTERSECT",VERTEX,{"derivedFrom":[subQ1,subQ0]});Q14=makeQuery(id+"F1.imprint","IMPRINT",FACE,{"disambiguationData":[TD([[makeQuery(id+"F1.imprint","IMPRINT",EDGE,{"disambiguationData":[TD([[subQ2,-1.0]])],"derivedFrom":subQ1}),-1.0]])]});}
            var Q15;
            {var subQ0=sQuery(id+"F1.wireOp",EDGE,"E34.1");var subQ1=sQuery(id+"F1.wireOp",EDGE,"E24");var subQ2=makeQuery(id+"F1.imprint","INTERSECT",VERTEX,{"derivedFrom":[subQ1,subQ0]});Q15=makeQuery(id+"F1.imprint","IMPRINT",FACE,{"disambiguationData":[TD([[makeQuery(id+"F1.imprint","IMPRINT",EDGE,{"disambiguationData":[TD([[subQ2,-1.0]])],"derivedFrom":subQ1}),1.0]])]});}
            extrude(context, id + "F4", {"entities" : qUnion([Q0, Q1, Q2, Q3, Q4, Q5, Q6, Q7, Q8, Q9, Q10, Q11, Q12, Q13, Q14, Q15]), "depth" : 3.17 * mm});
        }
        {
            var Q0;
            Q0=qCreatedBy(makeId("Top.planeOp"),FACE);
            var sketch = newSketch(context, id + "F5", { "sketchPlane" : qUnion([Q0])});
            skLineSegment(sketch, "E39.0", {"start": v(66.11, 6.05) * mm, "end": v(66.11, -52.37) * mm});
            skFitSpline(sketch, "E39.1", {"points": [v(52.67, -51.16) * mm, v(64.82, -54.87) * mm, v(80.4, -50.58) * mm, v(85.16, -44.23) * mm]});
            skLineSegment(sketch, "E39.2", {"start": v(52.67, -51.16) * mm, "end": v(-83.6, -9.5) * mm});
            skArc(sketch, "E39.3", {"start": v(-52.81, 15.65) * mm, "mid": v(-91.73, 31.87) * mm, "end": v(-83.6, -9.5) * mm});
            skFitSpline(sketch, "E39.4", {"points": [v(-52.81, 15.65) * mm, v(12.06, 14.43) * mm, v(24.52, 13.11) * mm, v(11.95, 42.23) * mm]});
            skArc(sketch, "E39.5", {"start": v(17.17, 35.44) * mm, "mid": v(15.59, 35.73) * mm, "end": v(14.99, 34.24) * mm});
            skArc(sketch, "E39.6", {"start": v(17.17, 35.44) * mm, "mid": v(39.22, 16.71) * mm, "end": v(66.11, 6.05) * mm});
            skCircle(sketch, "E40.0", {"center": v(-60.76, -4.74) * mm, "radius": 5.04 * mm});
            skCircle(sketch, "E40.1", {"center": v(-37.42, -11.87) * mm, "radius": 5.04 * mm});
            skCircle(sketch, "E40.2", {"center": v(-14.07, -19.01) * mm, "radius": 5.04 * mm});
            skCircle(sketch, "E40.3", {"center": v(9.27, -26.15) * mm, "radius": 5.04 * mm});
            skCircle(sketch, "E40.4", {"center": v(32.61, -33.28) * mm, "radius": 5.04 * mm});
            skCircle(sketch, "E40.5", {"center": v(55.95, -40.42) * mm, "radius": 5.04 * mm});
            skSolve(sketch);
        }
        {
            var Q0;
            Q0=makeQuery(id+"F5.imprint","IMPRINT",FACE,{"disambiguationData":[TD([[makeQuery(id+"F5.imprint","IMPRINT",EDGE,{"derivedFrom":sQuery(id+"F5.wireOp",EDGE,"E40.0")}),1.0]])]});
            var Q1;
            Q1=makeQuery(id+"F5.imprint","IMPRINT",FACE,{"disambiguationData":[TD([[makeQuery(id+"F5.imprint","IMPRINT",EDGE,{"derivedFrom":sQuery(id+"F5.wireOp",EDGE,"E40.1")}),1.0]])]});
            var Q2;
            Q2=makeQuery(id+"F5.imprint","IMPRINT",FACE,{"disambiguationData":[TD([[makeQuery(id+"F5.imprint","IMPRINT",EDGE,{"derivedFrom":sQuery(id+"F5.wireOp",EDGE,"E40.2")}),1.0]])]});
            var Q3;
            Q3=makeQuery(id+"F5.imprint","IMPRINT",FACE,{"disambiguationData":[TD([[makeQuery(id+"F5.imprint","IMPRINT",EDGE,{"derivedFrom":sQuery(id+"F5.wireOp",EDGE,"E40.3")}),1.0]])]});
            var Q4;
            Q4=makeQuery(id+"F5.imprint","IMPRINT",FACE,{"disambiguationData":[TD([[makeQuery(id+"F5.imprint","IMPRINT",EDGE,{"derivedFrom":sQuery(id+"F5.wireOp",EDGE,"E40.4")}),1.0]])]});
            var Q5;
            Q5=makeQuery(id+"F5.imprint","IMPRINT",FACE,{"disambiguationData":[TD([[makeQuery(id+"F5.imprint","IMPRINT",EDGE,{"derivedFrom":sQuery(id+"F5.wireOp",EDGE,"E40.5")}),1.0]])]});
            extrude(context, id + "F6", {"entities" : qUnion([Q0, Q1, Q2, Q3, Q4, Q5]), "operationType" : NewBodyOperationType.REMOVE, "endBound" : BoundingType.THROUGH_ALL, "depth" : 25.4 * mm});
        }
        {
            var Q0;
            Q0=makeQuery(id+"F4.opExtrude","SWEPT_EDGE",EDGE,{"disambiguationData":[OSD([sQuery(id+"F1.wireOp",EDGE,"E35.1"),sQuery(id+"F1.wireOp",EDGE,"E35.2")])]});
            fillet(context, id + "F7", {"entities" : qUnion([Q0]), "radius" : 1.27 * mm, "tangentPropagation" : true, "allowEdgeOverflow" : false});
        }
        {
            var Q0;
            Q0=qCreatedBy(makeId("Top.planeOp"),FACE);
            var sketch = newSketch(context, id + "F8", { "sketchPlane" : qUnion([Q0])});
            skLineSegment(sketch, "E41.0", {"start": v(-68.45, -21.17) * mm, "end": v(61.8, -21.17) * mm, "construction": true});
            skLineSegment(sketch, "E41.1", {"start": v(-91.8, 9.52) * mm, "end": v(75.82, 9.52) * mm, "construction": true});
            skLineSegment(sketch, "E42.bottom", {"start": v(35.79, -16.14) * mm, "end": v(29.44, -16.14) * mm});
            skLineSegment(sketch, "E42.top", {"start": v(35.79, -9.79) * mm, "end": v(29.44, -9.79) * mm});
            skLineSegment(sketch, "E42.left", {"start": v(35.79, -16.14) * mm, "end": v(35.79, -9.79) * mm});
            skLineSegment(sketch, "E42.right", {"start": v(29.44, -16.14) * mm, "end": v(29.44, -9.79) * mm});
            skPoint(sketch, "E42.middle", {"position": v(32.61, -12.96) * mm});
            skLineSegment(sketch, "E43.0", {"start": v(62.7, -4.76) * mm, "end": v(-45.1, -4.76) * mm, "construction": true});
            skLineSegment(sketch, "E44", {"start": v(32.61, -12.96) * mm, "end": v(18.74, -12.96) * mm, "construction": true});
            skPoint(sketch, "E45", {"position": v(32.61, -33.28) * mm});
            skSolve(sketch);
        }
        {
            var Q0;
            Q0 = qSketchRegion(id + "F8", true);
            extrude(context, id + "F9", {"entities" : qUnion([Q0]), "operationType" : NewBodyOperationType.REMOVE, "depth" : 25.4 * mm});
        }
    });
